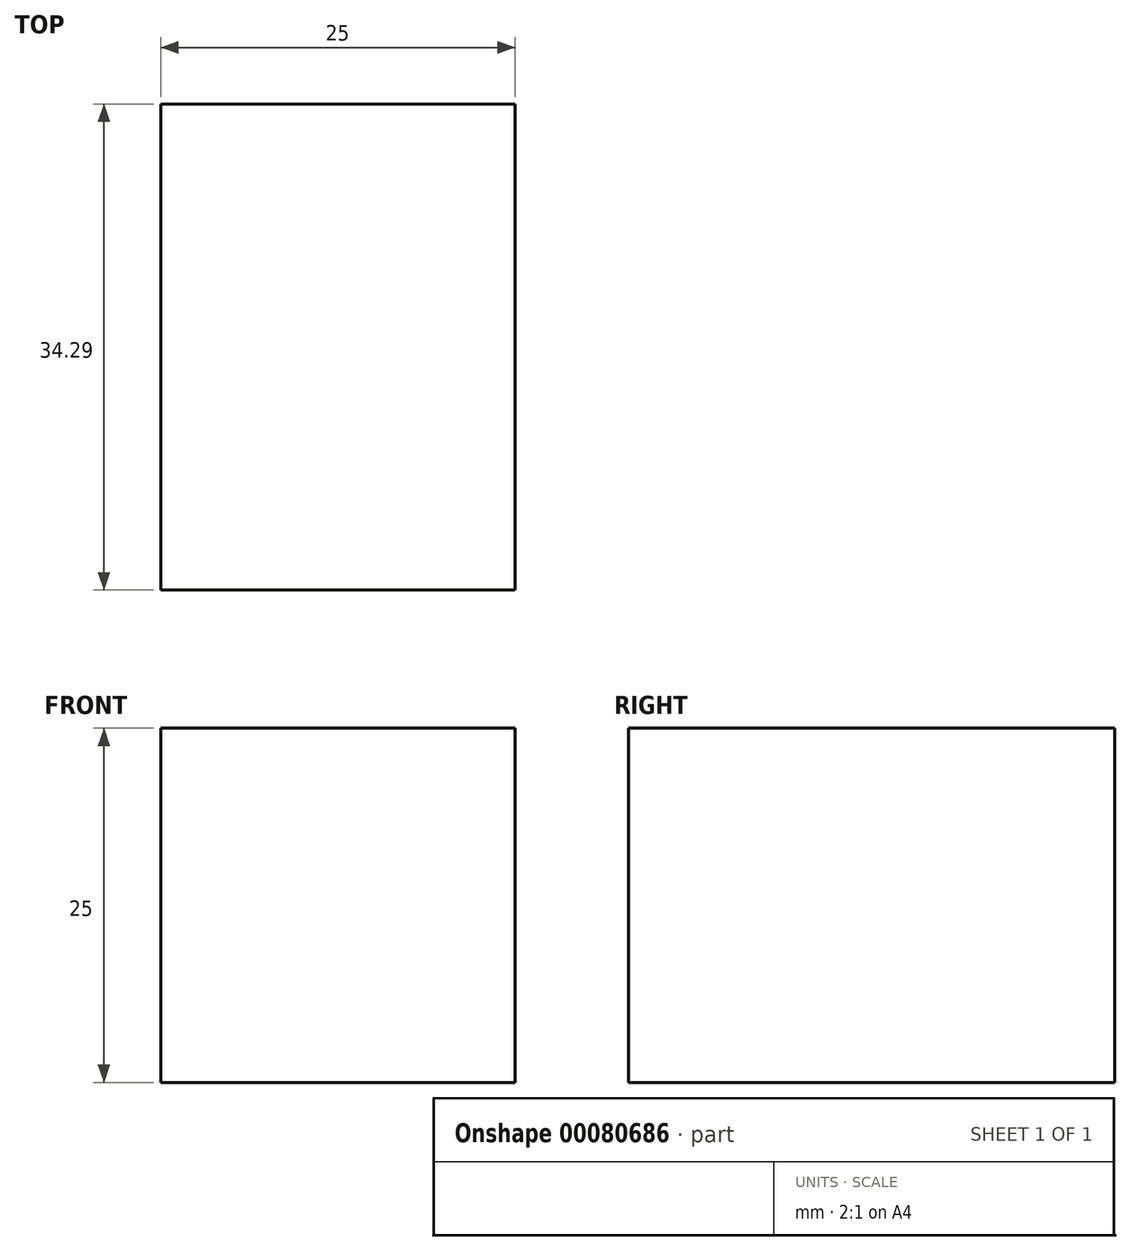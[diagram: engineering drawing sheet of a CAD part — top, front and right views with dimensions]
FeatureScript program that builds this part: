
annotation { "Feature Type Name" : "Feature", "Feature Type Description" : "" }
export const myFeature = defineFeature(function(context is Context, id is Id, definition is map)
    precondition{}
    {
        {
            var Q0;
            Q0=qCreatedBy(makeId("Front.planeOp"),FACE);
            var sketch = newSketch(context, id + "F0", { "sketchPlane" : qUnion([Q0])});
            skLineSegment(sketch, "E0.bottom", {"start": v(-12.5, 12.5) * mm, "end": v(12.5, 12.5) * mm});
            skLineSegment(sketch, "E0.top", {"start": v(-12.5, -12.5) * mm, "end": v(12.5, -12.5) * mm});
            skLineSegment(sketch, "E0.left", {"start": v(-12.5, 12.5) * mm, "end": v(-12.5, -12.5) * mm});
            skLineSegment(sketch, "E0.right", {"start": v(12.5, 12.5) * mm, "end": v(12.5, -12.5) * mm});
            skPoint(sketch, "E0.middle", {"position": v(0, 0) * mm});
            skSolve(sketch);
        }
        {
            var Q0;
            Q0=makeQuery(id+"F0.imprint","IMPRINT",FACE,{"disambiguationData":[TD([[makeQuery(id+"F0.imprint","IMPRINT",EDGE,{"derivedFrom":sQuery(id+"F0.wireOp",EDGE,"E0.bottom")}),-1.0]])]});
            extrude(context, id + "F1", {"entities" : qUnion([Q0]), "depth" : 34.3 * mm});
        }
    });
